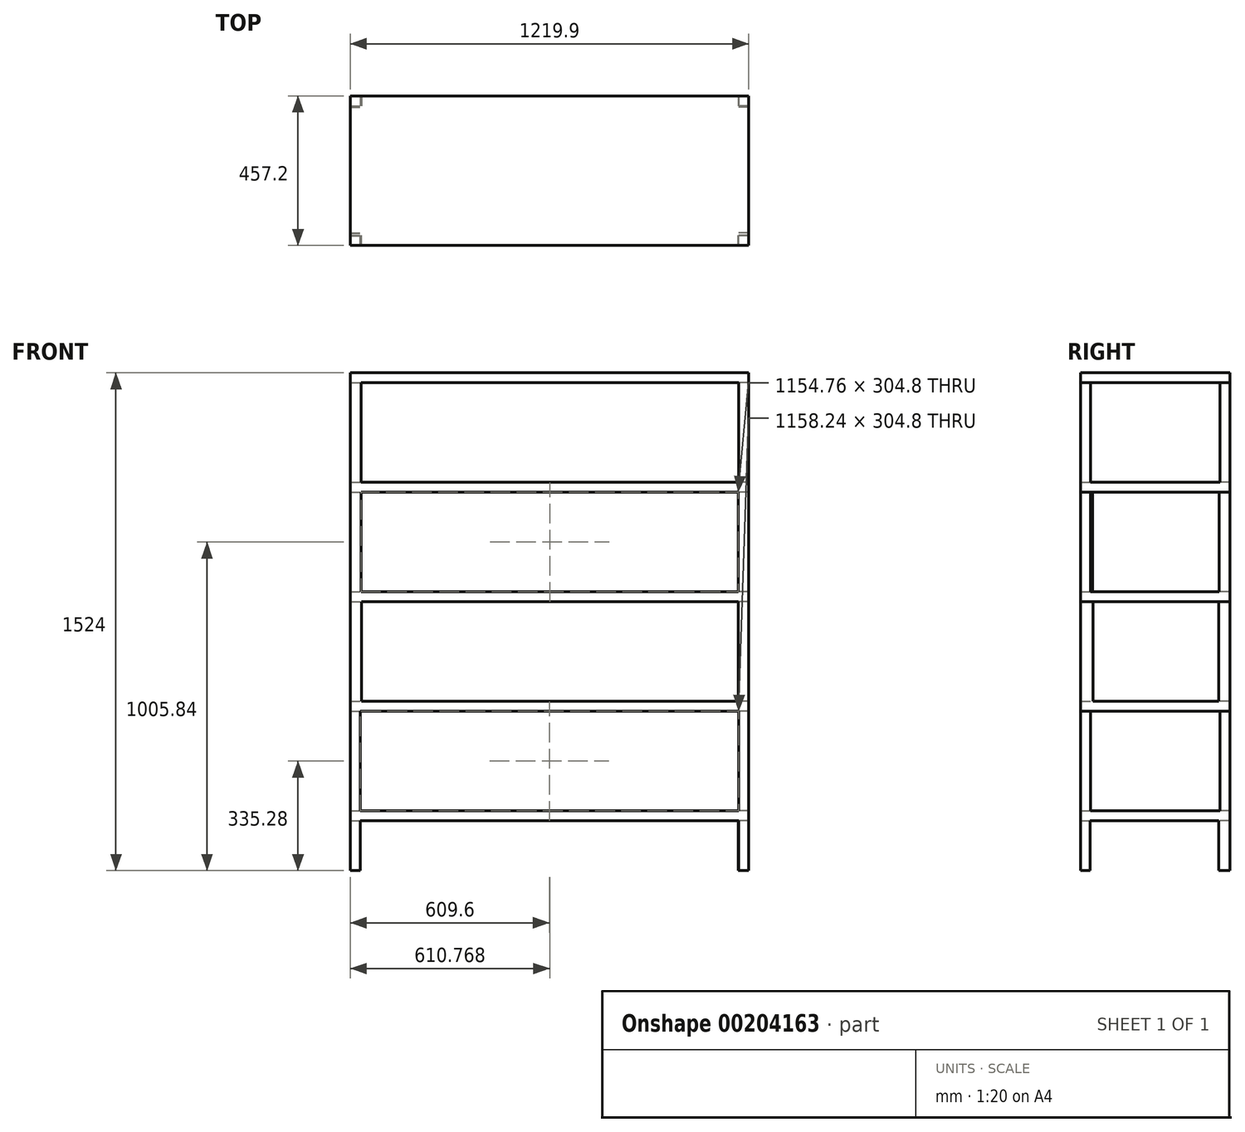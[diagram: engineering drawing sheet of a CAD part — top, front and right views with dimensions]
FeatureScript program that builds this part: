
annotation { "Feature Type Name" : "Feature", "Feature Type Description" : "" }
export const myFeature = defineFeature(function(context is Context, id is Id, definition is map)
    precondition{}
    {
        {
            var Q0;
            Q0=qCreatedBy(makeId("Top.planeOp"),FACE);
            var sketch = newSketch(context, id + "F0", { "sketchPlane" : qUnion([Q0])});
            skLineSegment(sketch, "E0.bottom", {"start": v(0, 0) * mm, "end": v(1219.2, 0) * mm});
            skLineSegment(sketch, "E0.top", {"start": v(0, 457.2) * mm, "end": v(1219.2, 457.2) * mm});
            skLineSegment(sketch, "E0.left", {"start": v(0, 0) * mm, "end": v(0, 457.2) * mm});
            skLineSegment(sketch, "E0.right", {"start": v(1219.2, 0) * mm, "end": v(1219.2, 457.2) * mm});
            skSolve(sketch);
        }
        {
            var Q0;
            Q0=makeQuery(id+"F0.imprint","IMPRINT",FACE,{"disambiguationData":[TD([[makeQuery(id+"F0.imprint","IMPRINT",EDGE,{"derivedFrom":sQuery(id+"F0.wireOp",EDGE,"E0.bottom")}),1.0]])]});
            extrude(context, id + "F1", {"entities" : qUnion([Q0]), "depth" : 30.48 * mm});
        }
        {
            var Q0;
            Q0=makeQuery(id+"F1.opExtrude","CAP_FACE",FACE,{"disambiguationData":[OSD([sQuery(id+"F0.wireOp",EDGE,"E0.bottom"),sQuery(id+"F0.wireOp",EDGE,"E0.top"),sQuery(id+"F0.wireOp",EDGE,"E0.left"),sQuery(id+"F0.wireOp",EDGE,"E0.right")])],"isStart":false});
            var sketch = newSketch(context, id + "F2", { "sketchPlane" : qUnion([Q0])});
            skLineSegment(sketch, "E1.bottom", {"start": v(0, 0) * mm, "end": v(30.48, 0) * mm});
            skLineSegment(sketch, "E1.top", {"start": v(0, 30.48) * mm, "end": v(30.48, 30.48) * mm});
            skLineSegment(sketch, "E1.left", {"start": v(0, 0) * mm, "end": v(0, 30.48) * mm});
            skLineSegment(sketch, "E1.right", {"start": v(30.48, 0) * mm, "end": v(30.48, 30.48) * mm});
            skLineSegment(sketch, "E2.bottom", {"start": v(0, 457.2) * mm, "end": v(30.48, 457.2) * mm});
            skLineSegment(sketch, "E2.top", {"start": v(0, 426.72) * mm, "end": v(30.48, 426.72) * mm});
            skLineSegment(sketch, "E2.left", {"start": v(0, 457.2) * mm, "end": v(0, 426.72) * mm});
            skLineSegment(sketch, "E2.right", {"start": v(30.48, 457.2) * mm, "end": v(30.48, 426.72) * mm});
            skLineSegment(sketch, "E3.bottom", {"start": v(1219.2, 457.2) * mm, "end": v(1188.72, 457.2) * mm});
            skLineSegment(sketch, "E3.top", {"start": v(1219.2, 426.72) * mm, "end": v(1188.72, 426.72) * mm});
            skLineSegment(sketch, "E3.left", {"start": v(1219.2, 457.2) * mm, "end": v(1219.2, 426.72) * mm});
            skLineSegment(sketch, "E3.right", {"start": v(1188.72, 457.2) * mm, "end": v(1188.72, 426.72) * mm});
            skLineSegment(sketch, "E4.bottom", {"start": v(1219.2, 0) * mm, "end": v(1188.72, 0) * mm});
            skLineSegment(sketch, "E4.top", {"start": v(1219.2, 30.48) * mm, "end": v(1188.72, 30.48) * mm});
            skLineSegment(sketch, "E4.left", {"start": v(1219.2, 0) * mm, "end": v(1219.2, 30.48) * mm});
            skLineSegment(sketch, "E4.right", {"start": v(1188.72, 0) * mm, "end": v(1188.72, 30.48) * mm});
            skSolve(sketch);
        }
        {
            var Q0;
            Q0 = qSketchRegion(id + "F2", true);
            extrude(context, id + "F3", {"entities" : qUnion([Q0]), "operationType" : NewBodyOperationType.ADD, "depth" : 304.8 * mm});
        }
        {
            var Q0;
            Q0=makeQuery(id+"F3.opExtrude","CAP_FACE",FACE,{"disambiguationData":[OSD([sQuery(id+"F2.wireOp",EDGE,"E2.bottom"),sQuery(id+"F2.wireOp",EDGE,"E2.top"),sQuery(id+"F2.wireOp",EDGE,"E2.left"),sQuery(id+"F2.wireOp",EDGE,"E2.right")])],"isStart":false});
            var sketch = newSketch(context, id + "F4", { "sketchPlane" : qUnion([Q0])});
            skLineSegment(sketch, "E5.bottom", {"start": v(0, 457.2) * mm, "end": v(1219.4, 457.2) * mm});
            skLineSegment(sketch, "E5.top", {"start": v(0, 0) * mm, "end": v(1219.4, 0) * mm});
            skLineSegment(sketch, "E5.left", {"start": v(0, 457.2) * mm, "end": v(0, 0) * mm});
            skLineSegment(sketch, "E5.right", {"start": v(1219.4, 457.2) * mm, "end": v(1219.4, 0) * mm});
            skSolve(sketch);
        }
        {
            var Q0;
            Q0 = qSketchRegion(id + "F4", true);
            extrude(context, id + "F5", {"entities" : qUnion([Q0]), "operationType" : NewBodyOperationType.ADD, "depth" : 30.48 * mm});
        }
        {
            var Q0;
            Q0=makeQuery(id+"F5.opExtrude","CAP_FACE",FACE,{"disambiguationData":[OSD([sQuery(id+"F4.wireOp",EDGE,"E5.bottom"),sQuery(id+"F4.wireOp",EDGE,"E5.top"),sQuery(id+"F4.wireOp",EDGE,"E5.left"),sQuery(id+"F4.wireOp",EDGE,"E5.right")])],"isStart":false});
            var sketch = newSketch(context, id + "F6", { "sketchPlane" : qUnion([Q0])});
            skLineSegment(sketch, "E6.bottom", {"start": v(0, 457.2) * mm, "end": v(34.83, 457.2) * mm});
            skLineSegment(sketch, "E6.top", {"start": v(0, 422.64) * mm, "end": v(34.83, 422.64) * mm});
            skLineSegment(sketch, "E6.left", {"start": v(0, 457.2) * mm, "end": v(0, 422.64) * mm});
            skLineSegment(sketch, "E6.right", {"start": v(34.83, 457.2) * mm, "end": v(34.83, 422.64) * mm});
            skLineSegment(sketch, "E7.bottom", {"start": v(0, 0) * mm, "end": v(34.83, 0) * mm});
            skLineSegment(sketch, "E7.top", {"start": v(0, 37.64) * mm, "end": v(34.83, 37.64) * mm});
            skLineSegment(sketch, "E7.left", {"start": v(0, 0) * mm, "end": v(0, 37.64) * mm});
            skLineSegment(sketch, "E7.right", {"start": v(34.83, 0) * mm, "end": v(34.83, 37.64) * mm});
            skLineSegment(sketch, "E8.bottom", {"start": v(1219.4, 0) * mm, "end": v(1187.15, 0) * mm});
            skLineSegment(sketch, "E8.top", {"start": v(1219.4, 37.64) * mm, "end": v(1187.15, 37.64) * mm});
            skLineSegment(sketch, "E8.left", {"start": v(1219.4, 0) * mm, "end": v(1219.4, 37.64) * mm});
            skLineSegment(sketch, "E8.right", {"start": v(1187.15, 0) * mm, "end": v(1187.15, 37.64) * mm});
            skLineSegment(sketch, "E9.bottom", {"start": v(1219.4, 457.2) * mm, "end": v(1187.15, 457.2) * mm});
            skLineSegment(sketch, "E9.top", {"start": v(1219.4, 422.64) * mm, "end": v(1187.15, 422.64) * mm});
            skLineSegment(sketch, "E9.left", {"start": v(1219.4, 457.2) * mm, "end": v(1219.4, 422.64) * mm});
            skLineSegment(sketch, "E9.right", {"start": v(1187.15, 457.2) * mm, "end": v(1187.15, 422.64) * mm});
            skSolve(sketch);
        }
        {
            var Q0;
            Q0 = qSketchRegion(id + "F6", true);
            extrude(context, id + "F7", {"entities" : qUnion([Q0]), "operationType" : NewBodyOperationType.ADD, "depth" : 304.8 * mm});
        }
        {
            var Q0;
            Q0=makeQuery(id+"F7.opExtrude","CAP_FACE",FACE,{"disambiguationData":[OSD([sQuery(id+"F6.wireOp",EDGE,"E6.bottom"),sQuery(id+"F6.wireOp",EDGE,"E6.top"),sQuery(id+"F6.wireOp",EDGE,"E6.left"),sQuery(id+"F6.wireOp",EDGE,"E6.right")])],"isStart":false});
            var sketch = newSketch(context, id + "F8", { "sketchPlane" : qUnion([Q0])});
            skLineSegment(sketch, "E10.bottom", {"start": v(0, 457.2) * mm, "end": v(1219.03, 457.2) * mm});
            skLineSegment(sketch, "E10.top", {"start": v(0, 0) * mm, "end": v(1219.03, 0) * mm});
            skLineSegment(sketch, "E10.left", {"start": v(0, 457.2) * mm, "end": v(0, 0) * mm});
            skLineSegment(sketch, "E10.right", {"start": v(1219.03, 457.2) * mm, "end": v(1219.03, 0) * mm});
            skSolve(sketch);
        }
        {
            var Q0;
            Q0 = qSketchRegion(id + "F8", true);
            extrude(context, id + "F9", {"entities" : qUnion([Q0]), "operationType" : NewBodyOperationType.ADD, "depth" : 30.48 * mm});
        }
        {
            var Q0;
            Q0=makeQuery(id+"F9.opExtrude","CAP_FACE",FACE,{"disambiguationData":[OSD([sQuery(id+"F8.wireOp",EDGE,"E10.bottom"),sQuery(id+"F8.wireOp",EDGE,"E10.top"),sQuery(id+"F8.wireOp",EDGE,"E10.left"),sQuery(id+"F8.wireOp",EDGE,"E10.right")])],"isStart":false});
            var sketch = newSketch(context, id + "F10", { "sketchPlane" : qUnion([Q0])});
            skLineSegment(sketch, "E11.bottom", {"start": v(0, 457.2) * mm, "end": v(33.39, 457.2) * mm});
            skLineSegment(sketch, "E11.top", {"start": v(0, 424.1) * mm, "end": v(33.39, 424.1) * mm});
            skLineSegment(sketch, "E11.left", {"start": v(0, 457.2) * mm, "end": v(0, 424.1) * mm});
            skLineSegment(sketch, "E11.right", {"start": v(33.39, 457.2) * mm, "end": v(33.39, 424.1) * mm});
            skLineSegment(sketch, "E12.bottom", {"start": v(0, 0) * mm, "end": v(33.39, 0) * mm});
            skLineSegment(sketch, "E12.top", {"start": v(0, 36.53) * mm, "end": v(33.39, 36.53) * mm});
            skLineSegment(sketch, "E12.left", {"start": v(0, 0) * mm, "end": v(0, 36.53) * mm});
            skLineSegment(sketch, "E12.right", {"start": v(33.39, 0) * mm, "end": v(33.39, 36.53) * mm});
            skLineSegment(sketch, "E13.bottom", {"start": v(1219.03, 0) * mm, "end": v(1188.15, 0) * mm});
            skLineSegment(sketch, "E13.top", {"start": v(1219.03, 30.55) * mm, "end": v(1188.15, 30.55) * mm});
            skLineSegment(sketch, "E13.left", {"start": v(1219.03, 0) * mm, "end": v(1219.03, 30.55) * mm});
            skLineSegment(sketch, "E13.right", {"start": v(1188.15, 0) * mm, "end": v(1188.15, 30.55) * mm});
            skLineSegment(sketch, "E14.bottom", {"start": v(1219.03, 457.2) * mm, "end": v(1188.15, 457.2) * mm});
            skLineSegment(sketch, "E14.top", {"start": v(1219.03, 424.1) * mm, "end": v(1188.15, 424.1) * mm});
            skLineSegment(sketch, "E14.left", {"start": v(1219.03, 457.2) * mm, "end": v(1219.03, 424.1) * mm});
            skLineSegment(sketch, "E14.right", {"start": v(1188.15, 457.2) * mm, "end": v(1188.15, 424.1) * mm});
            skSolve(sketch);
        }
        {
            var Q0;
            Q0 = qSketchRegion(id + "F10", true);
            extrude(context, id + "F11", {"entities" : qUnion([Q0]), "operationType" : NewBodyOperationType.ADD, "depth" : 304.8 * mm});
        }
        {
            var Q0;
            Q0=makeQuery(id+"F11.opExtrude","CAP_FACE",FACE,{"disambiguationData":[OSD([sQuery(id+"F10.wireOp",EDGE,"E11.bottom"),sQuery(id+"F10.wireOp",EDGE,"E11.top"),sQuery(id+"F10.wireOp",EDGE,"E11.left"),sQuery(id+"F10.wireOp",EDGE,"E11.right")])],"isStart":false});
            var sketch = newSketch(context, id + "F12", { "sketchPlane" : qUnion([Q0])});
            skLineSegment(sketch, "E15.bottom", {"start": v(0, 457.2) * mm, "end": v(1219.9, 457.2) * mm});
            skLineSegment(sketch, "E15.top", {"start": v(0, 0) * mm, "end": v(1219.9, 0) * mm});
            skLineSegment(sketch, "E15.left", {"start": v(0, 457.2) * mm, "end": v(0, 0) * mm});
            skLineSegment(sketch, "E15.right", {"start": v(1219.9, 457.2) * mm, "end": v(1219.9, 0) * mm});
            skSolve(sketch);
        }
        {
            var Q0;
            Q0 = qSketchRegion(id + "F12", true);
            extrude(context, id + "F13", {"entities" : qUnion([Q0]), "operationType" : NewBodyOperationType.ADD, "depth" : 30.48 * mm});
        }
        {
            var Q0;
            Q0=makeQuery(id+"F13.opExtrude","CAP_FACE",FACE,{"disambiguationData":[OSD([sQuery(id+"F12.wireOp",EDGE,"E15.bottom"),sQuery(id+"F12.wireOp",EDGE,"E15.top"),sQuery(id+"F12.wireOp",EDGE,"E15.left"),sQuery(id+"F12.wireOp",EDGE,"E15.right")])],"isStart":false});
            var sketch = newSketch(context, id + "F14", { "sketchPlane" : qUnion([Q0])});
            skLineSegment(sketch, "E16.bottom", {"start": v(0, 457.2) * mm, "end": v(30.47, 457.2) * mm});
            skLineSegment(sketch, "E16.top", {"start": v(0, 426.07) * mm, "end": v(30.47, 426.07) * mm});
            skLineSegment(sketch, "E16.left", {"start": v(0, 457.2) * mm, "end": v(0, 426.07) * mm});
            skLineSegment(sketch, "E16.right", {"start": v(30.47, 457.2) * mm, "end": v(30.47, 426.07) * mm});
            skLineSegment(sketch, "E17.bottom", {"start": v(0, 0) * mm, "end": v(32.84, 0) * mm});
            skLineSegment(sketch, "E17.top", {"start": v(0, 30.67) * mm, "end": v(32.84, 30.67) * mm});
            skLineSegment(sketch, "E17.left", {"start": v(0, 0) * mm, "end": v(0, 30.67) * mm});
            skLineSegment(sketch, "E17.right", {"start": v(32.84, 0) * mm, "end": v(32.84, 30.67) * mm});
            skLineSegment(sketch, "E18.bottom", {"start": v(1219.9, 0) * mm, "end": v(1189.26, 0) * mm});
            skLineSegment(sketch, "E18.top", {"start": v(1219.9, 30.67) * mm, "end": v(1189.26, 30.67) * mm});
            skLineSegment(sketch, "E18.left", {"start": v(1219.9, 0) * mm, "end": v(1219.9, 30.67) * mm});
            skLineSegment(sketch, "E18.right", {"start": v(1189.26, 0) * mm, "end": v(1189.26, 30.67) * mm});
            skLineSegment(sketch, "E19.bottom", {"start": v(1219.9, 457.2) * mm, "end": v(1189.26, 457.2) * mm});
            skLineSegment(sketch, "E19.top", {"start": v(1219.9, 426.76) * mm, "end": v(1189.26, 426.76) * mm});
            skLineSegment(sketch, "E19.left", {"start": v(1219.9, 457.2) * mm, "end": v(1219.9, 426.76) * mm});
            skLineSegment(sketch, "E19.right", {"start": v(1189.26, 457.2) * mm, "end": v(1189.26, 426.76) * mm});
            skSolve(sketch);
        }
        {
            var Q0;
            Q0 = qSketchRegion(id + "F14", true);
            extrude(context, id + "F15", {"entities" : qUnion([Q0]), "operationType" : NewBodyOperationType.ADD, "depth" : 304.8 * mm});
        }
        {
            var Q0;
            Q0=makeQuery(id+"F15.opExtrude","CAP_FACE",FACE,{"disambiguationData":[OSD([sQuery(id+"F14.wireOp",EDGE,"E16.bottom"),sQuery(id+"F14.wireOp",EDGE,"E16.top"),sQuery(id+"F14.wireOp",EDGE,"E16.left"),sQuery(id+"F14.wireOp",EDGE,"E16.right")])],"isStart":false});
            var sketch = newSketch(context, id + "F16", { "sketchPlane" : qUnion([Q0])});
            skLineSegment(sketch, "E20.bottom", {"start": v(0, 457.2) * mm, "end": v(1219.73, 457.2) * mm});
            skLineSegment(sketch, "E20.top", {"start": v(0, 0) * mm, "end": v(1219.73, 0) * mm});
            skLineSegment(sketch, "E20.left", {"start": v(0, 457.2) * mm, "end": v(0, 0) * mm});
            skLineSegment(sketch, "E20.right", {"start": v(1219.73, 457.2) * mm, "end": v(1219.73, 0) * mm});
            skSolve(sketch);
        }
        {
            var Q0;
            Q0 = qSketchRegion(id + "F16", true);
            extrude(context, id + "F17", {"entities" : qUnion([Q0]), "operationType" : NewBodyOperationType.ADD, "depth" : 30.48 * mm});
        }
        {
            var Q0;
            Q0=makeQuery(id+"F1.opExtrude","CAP_FACE",FACE,{"disambiguationData":[OSD([sQuery(id+"F0.wireOp",EDGE,"E0.bottom"),sQuery(id+"F0.wireOp",EDGE,"E0.top"),sQuery(id+"F0.wireOp",EDGE,"E0.left"),sQuery(id+"F0.wireOp",EDGE,"E0.right")])],"isStart":true});
            var sketch = newSketch(context, id + "F18", { "sketchPlane" : qUnion([Q0])});
            skLineSegment(sketch, "E21.bottom", {"start": v(0, 0) * mm, "end": v(30.17, 0) * mm});
            skLineSegment(sketch, "E21.top", {"start": v(0, -29.71) * mm, "end": v(30.17, -29.71) * mm});
            skLineSegment(sketch, "E21.left", {"start": v(0, 0) * mm, "end": v(0, -29.71) * mm});
            skLineSegment(sketch, "E21.right", {"start": v(30.17, 0) * mm, "end": v(30.17, -29.71) * mm});
            skPoint(sketch, "E22.oppositeSnap0", {"position": v(30.17, -14.86) * mm});
            skLineSegment(sketch, "E22.bottom", {"start": v(0, -457.2) * mm, "end": v(30.17, -457.2) * mm});
            skLineSegment(sketch, "E22.top", {"start": v(0, -423.58) * mm, "end": v(30.17, -423.58) * mm});
            skLineSegment(sketch, "E22.left", {"start": v(0, -457.2) * mm, "end": v(0, -423.58) * mm});
            skLineSegment(sketch, "E22.right", {"start": v(30.17, -457.2) * mm, "end": v(30.17, -423.58) * mm});
            skLineSegment(sketch, "E23.bottom", {"start": v(1219.2, -457.2) * mm, "end": v(1187.9, -457.2) * mm});
            skLineSegment(sketch, "E23.top", {"start": v(1219.2, -423.3) * mm, "end": v(1187.9, -423.3) * mm});
            skLineSegment(sketch, "E23.left", {"start": v(1219.2, -457.2) * mm, "end": v(1219.2, -423.3) * mm});
            skLineSegment(sketch, "E23.right", {"start": v(1187.9, -457.2) * mm, "end": v(1187.9, -423.3) * mm});
            skLineSegment(sketch, "E24.bottom", {"start": v(1219.2, 0) * mm, "end": v(1188.79, 0) * mm});
            skLineSegment(sketch, "E24.top", {"start": v(1219.2, -29.71) * mm, "end": v(1188.79, -29.71) * mm});
            skLineSegment(sketch, "E24.left", {"start": v(1219.2, 0) * mm, "end": v(1219.2, -29.71) * mm});
            skLineSegment(sketch, "E24.right", {"start": v(1188.79, 0) * mm, "end": v(1188.79, -29.71) * mm});
            skSolve(sketch);
        }
        {
            var Q0;
            Q0 = qSketchRegion(id + "F18", true);
            extrude(context, id + "F19", {"entities" : qUnion([Q0]), "operationType" : NewBodyOperationType.ADD, "depth" : 152.4 * mm});
        }
    });
